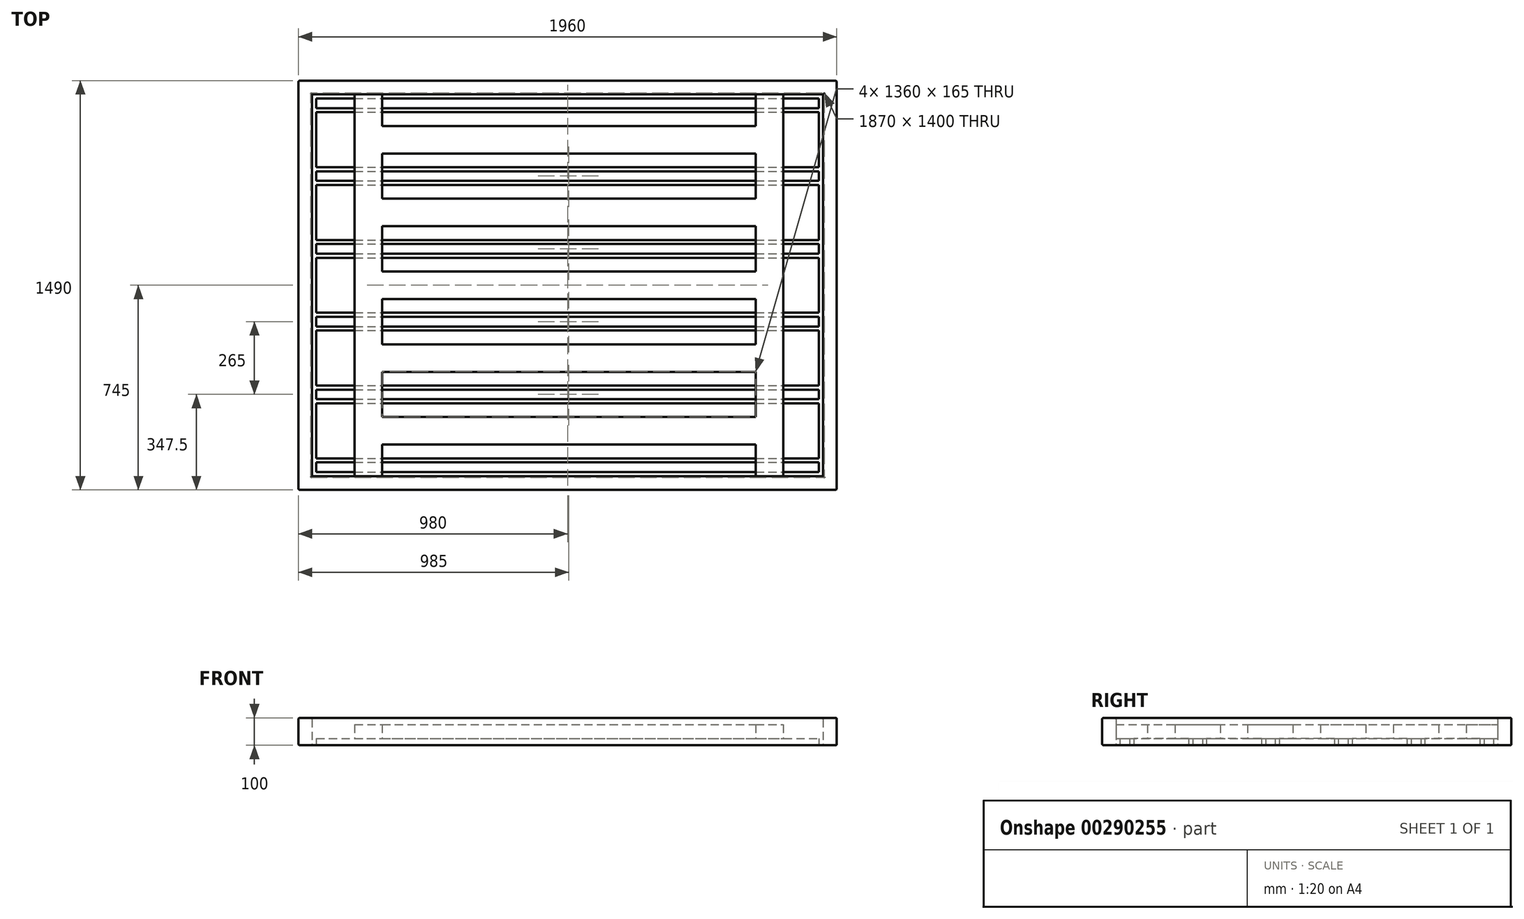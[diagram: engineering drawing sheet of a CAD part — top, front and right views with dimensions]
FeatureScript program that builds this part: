
annotation { "Feature Type Name" : "Feature", "Feature Type Description" : "" }
export const myFeature = defineFeature(function(context is Context, id is Id, definition is map)
    precondition{}
    {
        {
            var Q0;
            Q0=qCreatedBy(makeId("Top.planeOp"),FACE);
            var sketch = newSketch(context, id + "F0", { "sketchPlane" : qUnion([Q0])});
            skLineSegment(sketch, "E0.bottom", {"start": v(0, 0) * mm, "end": v(1960, 0) * mm});
            skLineSegment(sketch, "E0.top", {"start": v(0, 1490) * mm, "end": v(1960, 1490) * mm});
            skLineSegment(sketch, "E0.left", {"start": v(0, 0) * mm, "end": v(0, 1490) * mm});
            skLineSegment(sketch, "E0.right", {"start": v(1960, 0) * mm, "end": v(1960, 1490) * mm});
            skLineSegment(sketch, "E1.0", {"start": v(50, 1440) * mm, "end": v(1910, 1440) * mm});
            skLineSegment(sketch, "E1.1", {"start": v(50, 50) * mm, "end": v(50, 1440) * mm});
            skLineSegment(sketch, "E1.2", {"start": v(50, 50) * mm, "end": v(1910, 50) * mm});
            skLineSegment(sketch, "E1.3", {"start": v(1910, 50) * mm, "end": v(1910, 1440) * mm});
            skLineSegment(sketch, "E2.bottom", {"start": v(65, 65) * mm, "end": v(1895, 65) * mm});
            skLineSegment(sketch, "E2.top", {"start": v(65, 100) * mm, "end": v(1895, 100) * mm});
            skLineSegment(sketch, "E2.left", {"start": v(65, 65) * mm, "end": v(65, 100) * mm});
            skLineSegment(sketch, "E2.right", {"start": v(1895, 65) * mm, "end": v(1895, 100) * mm});
            skLineSegment(sketch, "E3.bottom", {"start": v(65, 315) * mm, "end": v(1895, 315) * mm});
            skLineSegment(sketch, "E3.top", {"start": v(65, 115) * mm, "end": v(1895, 115) * mm});
            skLineSegment(sketch, "E3.left", {"start": v(65, 315) * mm, "end": v(65, 115) * mm});
            skLineSegment(sketch, "E3.right", {"start": v(1895, 315) * mm, "end": v(1895, 115) * mm});
            skLineSegment(sketch, "E4.0.1.0", {"start": v(65, 580) * mm, "end": v(1895, 580) * mm});
            skLineSegment(sketch, "E4.0.1.1", {"start": v(1895, 580) * mm, "end": v(1895, 380) * mm});
            skLineSegment(sketch, "E4.0.1.2", {"start": v(65, 380) * mm, "end": v(1895, 380) * mm});
            skLineSegment(sketch, "E4.0.1.3", {"start": v(65, 580) * mm, "end": v(65, 380) * mm});
            skLineSegment(sketch, "E4.0.2.0", {"start": v(65, 845) * mm, "end": v(1895, 845) * mm});
            skLineSegment(sketch, "E4.0.2.1", {"start": v(1895, 845) * mm, "end": v(1895, 645) * mm});
            skLineSegment(sketch, "E4.0.2.2", {"start": v(65, 645) * mm, "end": v(1895, 645) * mm});
            skLineSegment(sketch, "E4.0.2.3", {"start": v(65, 845) * mm, "end": v(65, 645) * mm});
            skLineSegment(sketch, "E4.0.3.0", {"start": v(65, 1110) * mm, "end": v(1895, 1110) * mm});
            skLineSegment(sketch, "E4.0.3.1", {"start": v(1895, 1110) * mm, "end": v(1895, 910) * mm});
            skLineSegment(sketch, "E4.0.3.2", {"start": v(65, 910) * mm, "end": v(1895, 910) * mm});
            skLineSegment(sketch, "E4.0.3.3", {"start": v(65, 1110) * mm, "end": v(65, 910) * mm});
            skLineSegment(sketch, "E4.0.4.0", {"start": v(65, 1375) * mm, "end": v(1895, 1375) * mm});
            skLineSegment(sketch, "E4.0.4.1", {"start": v(1895, 1375) * mm, "end": v(1895, 1175) * mm});
            skLineSegment(sketch, "E4.0.4.2", {"start": v(65, 1175) * mm, "end": v(1895, 1175) * mm});
            skLineSegment(sketch, "E4.0.4.3", {"start": v(65, 1375) * mm, "end": v(65, 1175) * mm});
            skLineSegment(sketch, "E4.direction1", {"start": v(65, 115) * mm, "end": v(140, 115) * mm, "construction": true});
            skLineSegment(sketch, "E4.direction2", {"start": v(65, 115) * mm, "end": v(65, 380) * mm, "construction": true});
            skLineSegment(sketch, "E5.0.1.0", {"start": v(65, 330) * mm, "end": v(65, 365) * mm});
            skLineSegment(sketch, "E5.0.1.1", {"start": v(65, 365) * mm, "end": v(1895, 365) * mm});
            skLineSegment(sketch, "E5.0.1.2", {"start": v(65, 330) * mm, "end": v(1895, 330) * mm});
            skLineSegment(sketch, "E5.0.1.3", {"start": v(1895, 330) * mm, "end": v(1895, 365) * mm});
            skLineSegment(sketch, "E5.0.2.0", {"start": v(65, 595) * mm, "end": v(65, 630) * mm});
            skLineSegment(sketch, "E5.0.2.1", {"start": v(65, 630) * mm, "end": v(1895, 630) * mm});
            skLineSegment(sketch, "E5.0.2.2", {"start": v(65, 595) * mm, "end": v(1895, 595) * mm});
            skLineSegment(sketch, "E5.0.2.3", {"start": v(1895, 595) * mm, "end": v(1895, 630) * mm});
            skLineSegment(sketch, "E5.0.3.0", {"start": v(65, 860) * mm, "end": v(65, 895) * mm});
            skLineSegment(sketch, "E5.0.3.1", {"start": v(65, 895) * mm, "end": v(1895, 895) * mm});
            skLineSegment(sketch, "E5.0.3.2", {"start": v(65, 860) * mm, "end": v(1895, 860) * mm});
            skLineSegment(sketch, "E5.0.3.3", {"start": v(1895, 860) * mm, "end": v(1895, 895) * mm});
            skLineSegment(sketch, "E5.0.4.0", {"start": v(65, 1125) * mm, "end": v(65, 1160) * mm});
            skLineSegment(sketch, "E5.0.4.1", {"start": v(65, 1160) * mm, "end": v(1895, 1160) * mm});
            skLineSegment(sketch, "E5.0.4.2", {"start": v(65, 1125) * mm, "end": v(1895, 1125) * mm});
            skLineSegment(sketch, "E5.0.4.3", {"start": v(1895, 1125) * mm, "end": v(1895, 1160) * mm});
            skLineSegment(sketch, "E5.0.5.0", {"start": v(65, 1390) * mm, "end": v(65, 1425) * mm});
            skLineSegment(sketch, "E5.0.5.1", {"start": v(65, 1425) * mm, "end": v(1895, 1425) * mm});
            skLineSegment(sketch, "E5.0.5.2", {"start": v(65, 1390) * mm, "end": v(1895, 1390) * mm});
            skLineSegment(sketch, "E5.0.5.3", {"start": v(1895, 1390) * mm, "end": v(1895, 1425) * mm});
            skLineSegment(sketch, "E5.direction1", {"start": v(65, 65) * mm, "end": v(140, 65) * mm, "construction": true});
            skLineSegment(sketch, "E5.direction2", {"start": v(65, 65) * mm, "end": v(65, 330) * mm, "construction": true});
            skSolve(sketch);
        }
        {
            var Q0;
            Q0=makeQuery(id+"F0.imprint","IMPRINT",FACE,{"disambiguationData":[TD([[makeQuery(id+"F0.imprint","IMPRINT",EDGE,{"derivedFrom":sQuery(id+"F0.wireOp",EDGE,"E0.bottom")}),1.0]])]});
            extrude(context, id + "F1", {"entities" : qUnion([Q0]), "depth" : 100 * mm});
        }
        {
            var Q0;
            Q0=qSketchRegion(id+"F0",true);
            var Q1;
            Q1=makeQuery(id+"F0.imprint","IMPRINT",FACE,{"disambiguationData":[TD([[makeQuery(id+"F0.imprint","IMPRINT",EDGE,{"derivedFrom":sQuery(id+"F0.wireOp",EDGE,"E4.0.4.0")}),-1.0]])]});
            var Q2;
            Q2=makeQuery(id+"F0.imprint","IMPRINT",FACE,{"disambiguationData":[TD([[makeQuery(id+"F0.imprint","IMPRINT",EDGE,{"derivedFrom":sQuery(id+"F0.wireOp",EDGE,"E4.0.3.0")}),-1.0]])]});
            var Q3;
            Q3=makeQuery(id+"F0.imprint","IMPRINT",FACE,{"disambiguationData":[TD([[makeQuery(id+"F0.imprint","IMPRINT",EDGE,{"derivedFrom":sQuery(id+"F0.wireOp",EDGE,"E4.0.2.0")}),-1.0]])]});
            var Q4;
            Q4=makeQuery(id+"F0.imprint","IMPRINT",FACE,{"disambiguationData":[TD([[makeQuery(id+"F0.imprint","IMPRINT",EDGE,{"derivedFrom":sQuery(id+"F0.wireOp",EDGE,"E4.0.1.0")}),-1.0]])]});
            var Q5;
            Q5=makeQuery(id+"F0.imprint","IMPRINT",FACE,{"disambiguationData":[TD([[makeQuery(id+"F0.imprint","IMPRINT",EDGE,{"derivedFrom":sQuery(id+"F0.wireOp",EDGE,"E3.bottom")}),-1.0]])]});
            var Q6;
            Q6=makeQuery(id+"F0.imprint","IMPRINT",FACE,{"disambiguationData":[TD([[makeQuery(id+"F0.imprint","IMPRINT",EDGE,{"derivedFrom":sQuery(id+"F0.wireOp",EDGE,"E2.bottom")}),1.0]])]});
            var Q7;
            Q7=makeQuery(id+"F0.imprint","IMPRINT",FACE,{"disambiguationData":[TD([[makeQuery(id+"F0.imprint","IMPRINT",EDGE,{"derivedFrom":sQuery(id+"F0.wireOp",EDGE,"1c48348b-8a3d-41b5-89dd-84f6cd14f65a.0.1.0")}),1.0]])]});
            var Q8;
            Q8=makeQuery(id+"F0.imprint","IMPRINT",FACE,{"disambiguationData":[TD([[makeQuery(id+"F0.imprint","IMPRINT",EDGE,{"derivedFrom":sQuery(id+"F0.wireOp",EDGE,"1c48348b-8a3d-41b5-89dd-84f6cd14f65a.0.2.0")}),1.0]])]});
            var Q9;
            Q9=makeQuery(id+"F0.imprint","IMPRINT",FACE,{"disambiguationData":[TD([[makeQuery(id+"F0.imprint","IMPRINT",EDGE,{"derivedFrom":sQuery(id+"F0.wireOp",EDGE,"1c48348b-8a3d-41b5-89dd-84f6cd14f65a.0.3.0")}),1.0]])]});
            var Q10;
            Q10=makeQuery(id+"F0.imprint","IMPRINT",FACE,{"disambiguationData":[TD([[makeQuery(id+"F0.imprint","IMPRINT",EDGE,{"derivedFrom":sQuery(id+"F0.wireOp",EDGE,"1c48348b-8a3d-41b5-89dd-84f6cd14f65a.0.4.0")}),1.0]])]});
            var Q11;
            Q11=makeQuery(id+"F0.imprint","IMPRINT",FACE,{"disambiguationData":[TD([[makeQuery(id+"F0.imprint","IMPRINT",EDGE,{"derivedFrom":sQuery(id+"F0.wireOp",EDGE,"1c48348b-8a3d-41b5-89dd-84f6cd14f65a.0.5.0")}),1.0]])]});
            var Q12;
            Q12=makeQuery(id+"F0.imprint","IMPRINT",FACE,{"disambiguationData":[TD([[makeQuery(id+"F0.imprint","IMPRINT",EDGE,{"derivedFrom":sQuery(id+"F0.wireOp",EDGE,"E5.0.1.0")}),-1.0]])]});
            var Q13;
            Q13=makeQuery(id+"F0.imprint","IMPRINT",FACE,{"disambiguationData":[TD([[makeQuery(id+"F0.imprint","IMPRINT",EDGE,{"derivedFrom":sQuery(id+"F0.wireOp",EDGE,"E5.0.2.0")}),-1.0]])]});
            var Q14;
            Q14=makeQuery(id+"F0.imprint","IMPRINT",FACE,{"disambiguationData":[TD([[makeQuery(id+"F0.imprint","IMPRINT",EDGE,{"derivedFrom":sQuery(id+"F0.wireOp",EDGE,"E5.0.3.0")}),-1.0]])]});
            var Q15;
            Q15=makeQuery(id+"F0.imprint","IMPRINT",FACE,{"disambiguationData":[TD([[makeQuery(id+"F0.imprint","IMPRINT",EDGE,{"derivedFrom":sQuery(id+"F0.wireOp",EDGE,"E5.0.4.0")}),-1.0]])]});
            var Q16;
            Q16=makeQuery(id+"F0.imprint","IMPRINT",FACE,{"disambiguationData":[TD([[makeQuery(id+"F0.imprint","IMPRINT",EDGE,{"derivedFrom":sQuery(id+"F0.wireOp",EDGE,"E5.0.5.0")}),-1.0]])]});
            extrude(context, id + "F2", {"entities" : qUnion([Q0, Q1, Q2, Q3, Q4, Q5, Q6, Q7, Q8, Q9, Q10, Q11, Q12, Q13, Q14, Q15, Q16]), "operationType" : NewBodyOperationType.ADD, "depth" : 25 * mm});
        }
        {
            var Q0;
            Q0=makeQuery(id+"F1.opExtrude","CAP_EDGE",EDGE,{"disambiguationData":[OSD([sQuery(id+"F0.wireOp",EDGE,"E1.0")])],"isStart":false});
            var Q1;
            Q1=makeQuery(id+"F1.opExtrude","CAP_EDGE",EDGE,{"disambiguationData":[OSD([sQuery(id+"F0.wireOp",EDGE,"E1.1")])],"isStart":false});
            var Q2;
            Q2=makeQuery(id+"F1.opExtrude","CAP_EDGE",EDGE,{"disambiguationData":[OSD([sQuery(id+"F0.wireOp",EDGE,"E1.2")])],"isStart":false});
            var Q3;
            Q3=makeQuery(id+"F1.opExtrude","CAP_EDGE",EDGE,{"disambiguationData":[OSD([sQuery(id+"F0.wireOp",EDGE,"E1.3")])],"isStart":false});
            fillet(context, id + "F3", {"entities" : qUnion([Q0, Q1, Q2, Q3]), "radius" : 5 * mm, "tangentPropagation" : true, "allowEdgeOverflow" : false});
        }
        {
            var Q0;
            Q0=makeQuery(id+"F1.opExtrude","CAP_EDGE",EDGE,{"disambiguationData":[OSD([sQuery(id+"F0.wireOp",EDGE,"E0.top")])],"isStart":false});
            var Q1;
            Q1=makeQuery(id+"F1.opExtrude","CAP_EDGE",EDGE,{"disambiguationData":[OSD([sQuery(id+"F0.wireOp",EDGE,"E0.left")])],"isStart":false});
            var Q2;
            Q2=makeQuery(id+"F1.opExtrude","CAP_EDGE",EDGE,{"disambiguationData":[OSD([sQuery(id+"F0.wireOp",EDGE,"E0.right")])],"isStart":false});
            var Q3;
            Q3=makeQuery(id+"F1.opExtrude","CAP_EDGE",EDGE,{"disambiguationData":[OSD([sQuery(id+"F0.wireOp",EDGE,"E0.bottom")])],"isStart":false});
            var Q4;
            Q4=makeQuery(id+"F1.opExtrude","SWEPT_EDGE",EDGE,{"disambiguationData":[OSD([sQuery(id+"F0.wireOp",EDGE,"E0.bottom"),sQuery(id+"F0.wireOp",EDGE,"E0.right")])]});
            var Q5;
            Q5=makeQuery(id+"F1.opExtrude","SWEPT_EDGE",EDGE,{"disambiguationData":[OSD([sQuery(id+"F0.wireOp",EDGE,"E0.bottom"),sQuery(id+"F0.wireOp",EDGE,"E0.left")])]});
            var Q6;
            Q6=makeQuery(id+"F1.opExtrude","CAP_EDGE",EDGE,{"disambiguationData":[OSD([sQuery(id+"F0.wireOp",EDGE,"E0.bottom")])],"isStart":true});
            var Q7;
            Q7=makeQuery(id+"F1.opExtrude","CAP_EDGE",EDGE,{"disambiguationData":[OSD([sQuery(id+"F0.wireOp",EDGE,"E0.left")])],"isStart":true});
            var Q8;
            Q8=makeQuery(id+"F1.opExtrude","SWEPT_EDGE",EDGE,{"disambiguationData":[OSD([sQuery(id+"F0.wireOp",EDGE,"E0.top"),sQuery(id+"F0.wireOp",EDGE,"E0.left")])]});
            var Q9;
            Q9=makeQuery(id+"F1.opExtrude","CAP_EDGE",EDGE,{"disambiguationData":[OSD([sQuery(id+"F0.wireOp",EDGE,"E0.top")])],"isStart":true});
            var Q10;
            Q10=makeQuery(id+"F1.opExtrude","SWEPT_EDGE",EDGE,{"disambiguationData":[OSD([sQuery(id+"F0.wireOp",EDGE,"E0.top"),sQuery(id+"F0.wireOp",EDGE,"E0.right")])]});
            var Q11;
            Q11=makeQuery(id+"F1.opExtrude","CAP_EDGE",EDGE,{"disambiguationData":[OSD([sQuery(id+"F0.wireOp",EDGE,"E0.right")])],"isStart":true});
            var Q12;
            Q12=makeQuery(id+"F1.opExtrude","CAP_EDGE",EDGE,{"disambiguationData":[OSD([sQuery(id+"F0.wireOp",EDGE,"E1.1")])],"isStart":true});
            var Q13;
            Q13=makeQuery(id+"F1.opExtrude","CAP_EDGE",EDGE,{"disambiguationData":[OSD([sQuery(id+"F0.wireOp",EDGE,"E1.0")])],"isStart":true});
            var Q14;
            Q14=makeQuery(id+"F1.opExtrude","CAP_EDGE",EDGE,{"disambiguationData":[OSD([sQuery(id+"F0.wireOp",EDGE,"E1.2")])],"isStart":true});
            var Q15;
            Q15=makeQuery(id+"F1.opExtrude","CAP_EDGE",EDGE,{"disambiguationData":[OSD([sQuery(id+"F0.wireOp",EDGE,"E1.3")])],"isStart":true});
            fillet(context, id + "F4", {"entities" : qUnion([Q0, Q1, Q2, Q3, Q4, Q5, Q6, Q7, Q8, Q9, Q10, Q11, Q12, Q13, Q14, Q15]), "radius" : 5 * mm, "tangentPropagation" : true, "allowEdgeOverflow" : false});
        }
        {
            var Q0;
            Q0=makeQuery(id+"F2.opExtrude","CAP_FACE",FACE,{"disambiguationData":[OSD([sQuery(id+"F0.wireOp",EDGE,"E4.0.4.0"),sQuery(id+"F0.wireOp",EDGE,"E4.0.4.1"),sQuery(id+"F0.wireOp",EDGE,"E4.0.4.2"),sQuery(id+"F0.wireOp",EDGE,"E4.0.4.3")])],"isStart":false});
            var sketch = newSketch(context, id + "F5", { "sketchPlane" : qUnion([Q0])});
            skLineSegment(sketch, "E6.bottom", {"start": v(205, 50) * mm, "end": v(305, 50) * mm});
            skLineSegment(sketch, "E6.top", {"start": v(205, 1440) * mm, "end": v(305, 1440) * mm});
            skLineSegment(sketch, "E6.left", {"start": v(205, 50) * mm, "end": v(205, 1440) * mm});
            skLineSegment(sketch, "E6.right", {"start": v(305, 50) * mm, "end": v(305, 165) * mm});
            skLineSegment(sketch, "E7.1.0.0", {"start": v(1665, 50) * mm, "end": v(1665, 165) * mm});
            skLineSegment(sketch, "E7.1.0.1", {"start": v(1665, 1440) * mm, "end": v(1765, 1440) * mm});
            skLineSegment(sketch, "E7.1.0.2", {"start": v(1765, 50) * mm, "end": v(1765, 1440) * mm});
            skLineSegment(sketch, "E7.1.0.3", {"start": v(1665, 50) * mm, "end": v(1765, 50) * mm});
            skLineSegment(sketch, "E7.direction1", {"start": v(205, 50) * mm, "end": v(1665, 50) * mm, "construction": true});
            skLineSegment(sketch, "E8.bottom", {"start": v(305, 165) * mm, "end": v(1665, 165) * mm});
            skLineSegment(sketch, "E8.top", {"start": v(305, 265) * mm, "end": v(1665, 265) * mm});
            skLineSegment(sketch, "E9.trimOffspring", {"start": v(305, 265) * mm, "end": v(305, 430) * mm});
            skLineSegment(sketch, "E10.trimOffspring", {"start": v(1665, 265) * mm, "end": v(1665, 430) * mm});
            skLineSegment(sketch, "E11.0.1.0", {"start": v(305, 430) * mm, "end": v(1665, 430) * mm});
            skLineSegment(sketch, "E11.0.1.1", {"start": v(305, 530) * mm, "end": v(1665, 530) * mm});
            skLineSegment(sketch, "E11.0.2.0", {"start": v(305, 695) * mm, "end": v(1665, 695) * mm});
            skLineSegment(sketch, "E11.0.2.1", {"start": v(305, 795) * mm, "end": v(1665, 795) * mm});
            skLineSegment(sketch, "E11.0.3.0", {"start": v(305, 960) * mm, "end": v(1665, 960) * mm});
            skLineSegment(sketch, "E11.0.3.1", {"start": v(305, 1060) * mm, "end": v(1665, 1060) * mm});
            skLineSegment(sketch, "E11.0.4.0", {"start": v(305, 1225) * mm, "end": v(1665, 1225) * mm});
            skLineSegment(sketch, "E11.0.4.1", {"start": v(305, 1325) * mm, "end": v(1665, 1325) * mm});
            skLineSegment(sketch, "E11.direction1", {"start": v(305, 165) * mm, "end": v(330, 165) * mm, "construction": true});
            skLineSegment(sketch, "E11.direction2", {"start": v(305, 165) * mm, "end": v(305, 430) * mm, "construction": true});
            skLineSegment(sketch, "E12.trimOffspring", {"start": v(305, 530) * mm, "end": v(305, 695) * mm});
            skLineSegment(sketch, "E13.trimOffspring", {"start": v(305, 795) * mm, "end": v(305, 960) * mm});
            skLineSegment(sketch, "E14.trimOffspring", {"start": v(305, 1060) * mm, "end": v(305, 1225) * mm});
            skLineSegment(sketch, "E15.trimOffspring", {"start": v(305, 1325) * mm, "end": v(305, 1440) * mm});
            skLineSegment(sketch, "E16.trimOffspring", {"start": v(1665, 1325) * mm, "end": v(1665, 1440) * mm});
            skLineSegment(sketch, "E17.trimOffspring", {"start": v(1665, 1060) * mm, "end": v(1665, 1225) * mm});
            skLineSegment(sketch, "E18.trimOffspring", {"start": v(1665, 795) * mm, "end": v(1665, 960) * mm});
            skLineSegment(sketch, "E19.trimOffspring", {"start": v(1665, 530) * mm, "end": v(1665, 695) * mm});
            skSolve(sketch);
        }
        {
            var Q0;
            Q0=qSketchRegion(id+"F5",true);
            extrude(context, id + "F6", {"entities" : qUnion([Q0]), "depth" : 50 * mm});
        }
    });
